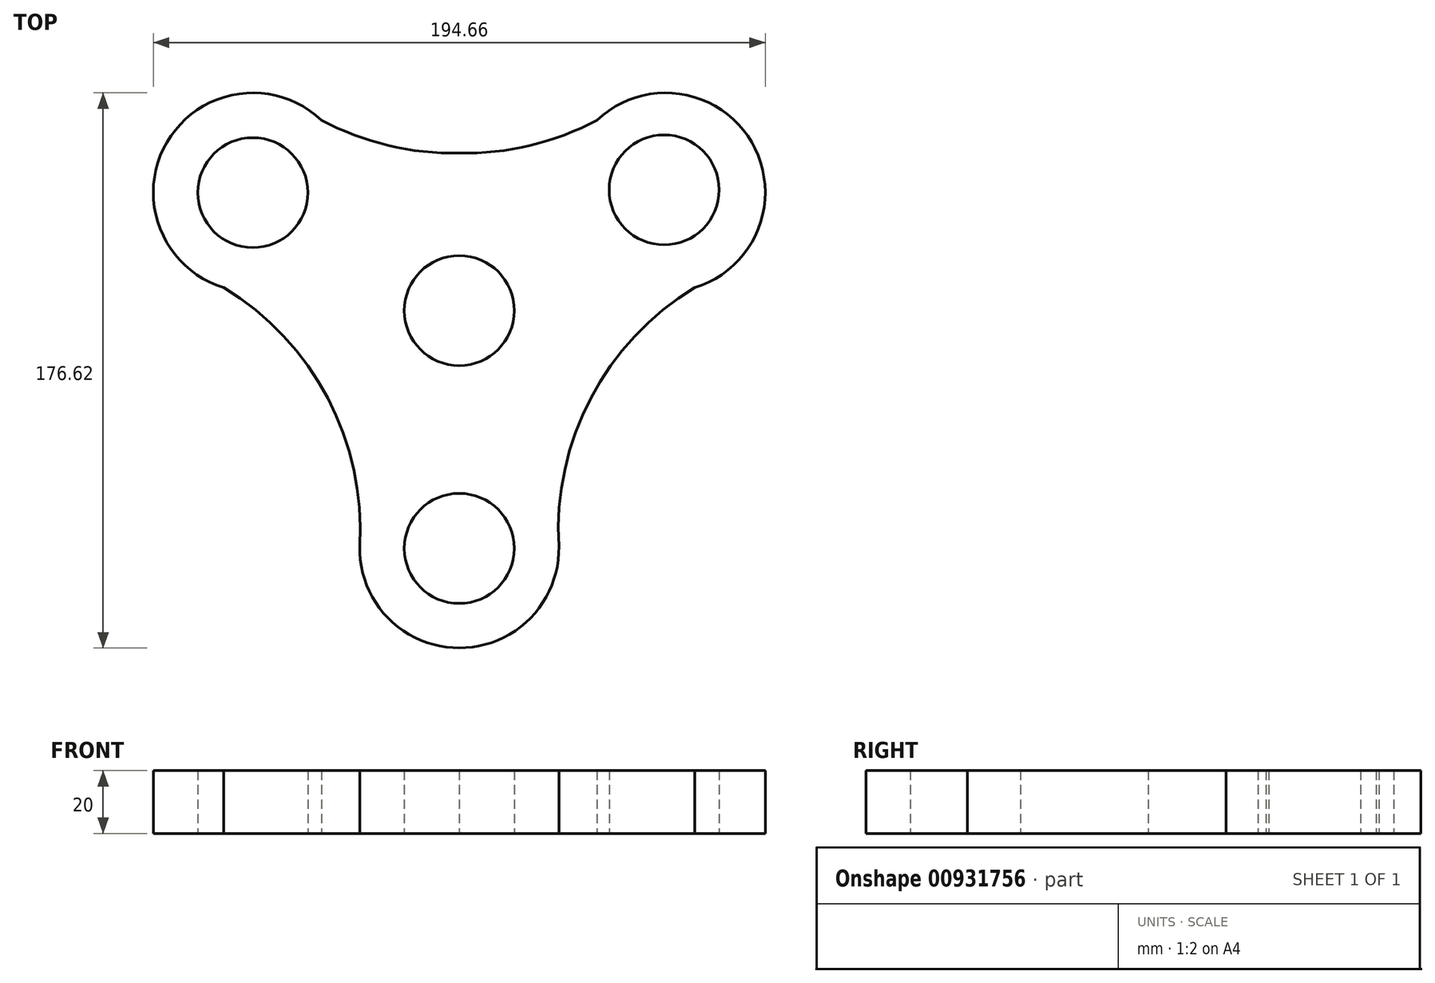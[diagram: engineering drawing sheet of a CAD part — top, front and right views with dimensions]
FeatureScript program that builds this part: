
annotation { "Feature Type Name" : "Feature", "Feature Type Description" : "" }
export const myFeature = defineFeature(function(context is Context, id is Id, definition is map)
    precondition{}
    {
        {
            var Q0;
            Q0=qCreatedBy(makeId("Top.planeOp"),FACE);
            var sketch = newSketch(context, id + "F0", { "sketchPlane" : qUnion([Q0])});
            skCircle(sketch, "E0.MirrorC", {"center": v(-65.69, 37.54) * mm, "radius": 17.5 * mm});
            skCircle(sketch, "E1", {"center": v(0, -75.65) * mm, "radius": 17.5 * mm});
            skCircle(sketch, "E2", {"center": v(0, 0) * mm, "radius": 107.34 * mm});
            skArc(sketch, "E3", {"start": v(-31.59, -73.18) * mm, "mid": v(0.04, -107.34) * mm, "end": v(31.58, -73.1) * mm});
            skArc(sketch, "E4", {"start": v(-43.86, 60.6) * mm, "mid": v(-93.02, 53.57) * mm, "end": v(-74.95, 7.31) * mm});
            skArc(sketch, "E5", {"start": v(-31.68, -75.03) * mm, "mid": v(-41.85, -27.84) * mm, "end": v(-74.95, 7.31) * mm});
            skPoint(sketch, "E6.orphan", {"position": v(75, 7.25) * mm});
            skPoint(sketch, "E7.orphan", {"position": v(31.18, -69.43) * mm});
            skCircle(sketch, "E8.MirrorC", {"center": v(65.18, 38.4) * mm, "radius": 17.5 * mm});
            skArc(sketch, "E9.MirrorCS", {"start": v(0, 50.1) * mm, "mid": v(-22.87, 52.62) * mm, "end": v(-44.35, 60.86) * mm});
            skCircle(sketch, "E10", {"center": v(0, 0) * mm, "radius": 17.5 * mm});
            skLineSegment(sketch, "E11", {"start": v(0, 0) * mm, "end": v(0, -75.65) * mm});
            skArc(sketch, "E12.MirrorCS", {"start": v(31.68, -75.03) * mm, "mid": v(41.85, -27.84) * mm, "end": v(74.95, 7.31) * mm});
            skLineSegment(sketch, "E13", {"start": v(0, 0) * mm, "end": v(0, 50.1) * mm});
            skArc(sketch, "E14.MirrorCS", {"start": v(0, 50.1) * mm, "mid": v(22.87, 52.62) * mm, "end": v(44.35, 60.86) * mm});
            skArc(sketch, "E15.MirrorCS", {"start": v(43.86, 60.6) * mm, "mid": v(93.02, 53.57) * mm, "end": v(74.95, 7.31) * mm});
            skSolve(sketch);
        }
        {
            var Q0;
            Q0=makeQuery(id+"F0.imprint","IMPRINT",FACE,{"disambiguationData":[TD([[makeQuery(id+"F0.imprint","IMPRINT",EDGE,{"derivedFrom":sQuery(id+"F0.wireOp",EDGE,"E1")}),-1.0]])]});
            extrude(context, id + "F1", {"entities" : qUnion([Q0]), "depth" : 20 * mm, "offsetDistance" : 25 * mm});
        }
    });
